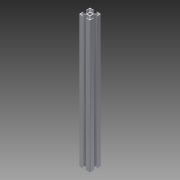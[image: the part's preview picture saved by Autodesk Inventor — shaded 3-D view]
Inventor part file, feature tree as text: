
AUTODESK INVENTOR PART (.ipt)
format: ipt  version: 2015 (Build 190159000, 159)  size: 173,056 bytes
history: native  units: mm
features: extrude x1, fillet x1, sketch x1
ambient origin geometry x8: Origin, YZ Plane, XZ Plane, XY Plane, X Axis, Y Axis, Z Axis, Center Point
bodies: Solid1 (feature_tree)
feature tree (3):
  extrude  "Extrusion1"  Depth=20.0mm
  fillet  "Fillet1"  Radius=5.0mm
  sketch  "Sketch1"  dims[d3=20.0mm d4=20.0mm d5=5.0mm d10=1.2mm d12=1.2mm d13=1.2mm d14=1.2mm d16=20.0mm d17=1.2mm d18=1.2mm d19=1.2mm d20=1.2mm d21=1.2mm d22=20.0mm d23=240.0mm d24=0.0mm d25=0.5mm]
